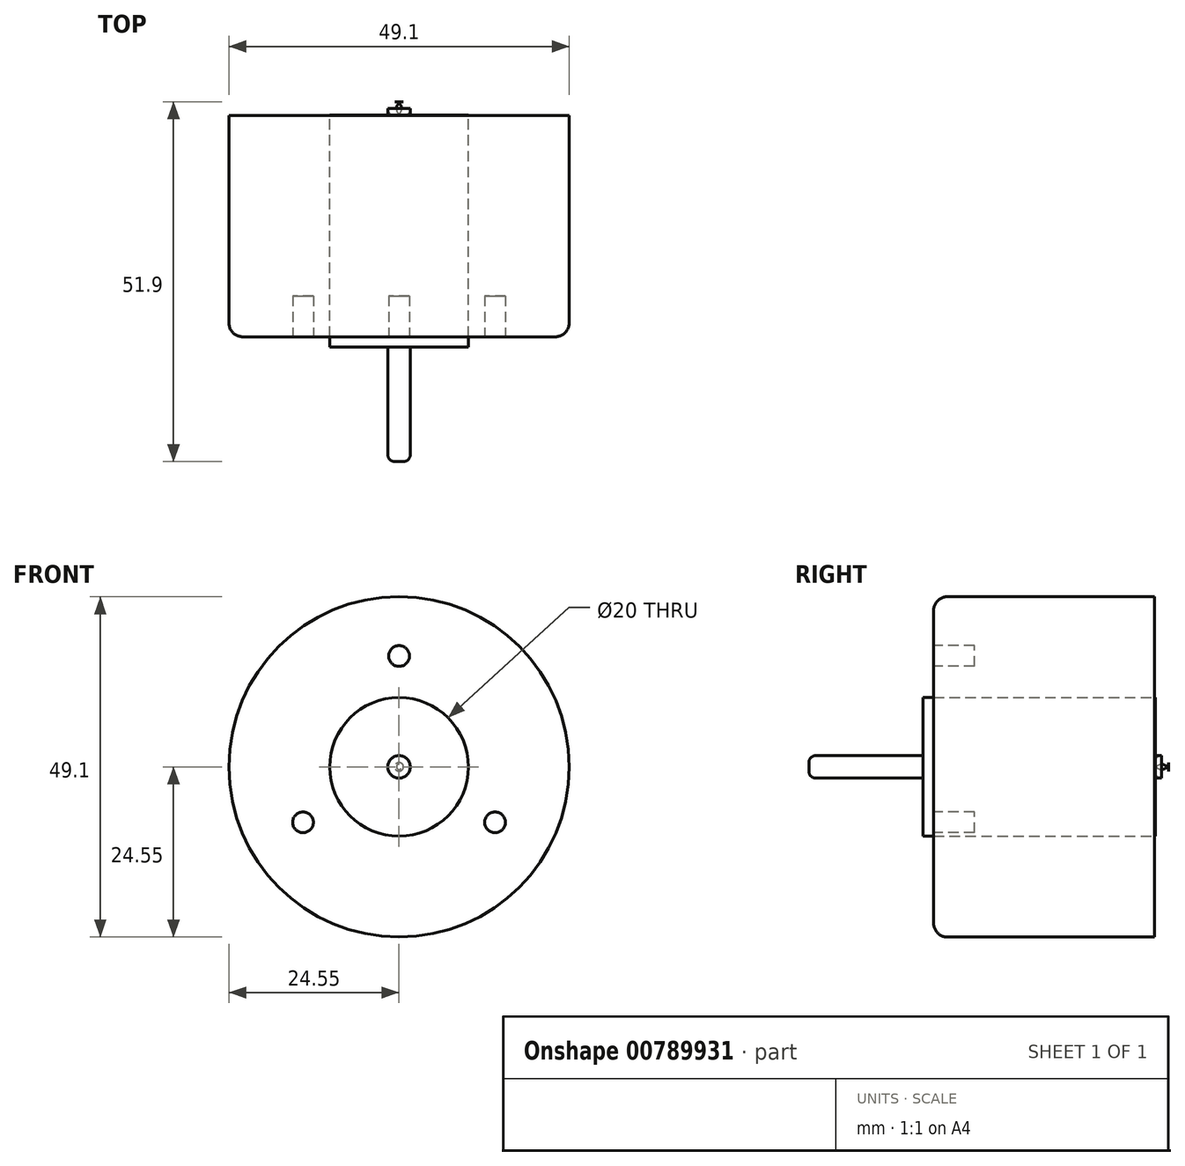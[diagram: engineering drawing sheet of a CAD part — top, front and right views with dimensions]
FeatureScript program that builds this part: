
annotation { "Feature Type Name" : "Feature", "Feature Type Description" : "" }
export const myFeature = defineFeature(function(context is Context, id is Id, definition is map)
    precondition{}
    {
        {
            var Q0;
            Q0=qCreatedBy(makeId("Front.planeOp"),FACE);
            var sketch = newSketch(context, id + "F0", { "sketchPlane" : qUnion([Q0])});
            skCircle(sketch, "E0", {"center": v(0, 0) * mm, "radius": 24.55 * mm});
            skCircle(sketch, "E1", {"center": v(0, 0) * mm, "radius": 10 * mm});
            skSolve(sketch);
        }
        {
            var Q0;
            Q0=makeQuery(id+"F0.imprint","IMPRINT",FACE,{"disambiguationData":[TD([[makeQuery(id+"F0.imprint","IMPRINT",EDGE,{"derivedFrom":sQuery(id+"F0.wireOp",EDGE,"E0")}),1.0]])]});
            extrude(context, id + "F1", {"entities" : qUnion([Q0]), "oppositeDirection" : true, "depth" : 31.9 * mm, "offsetDistance" : 25 * mm});
        }
        {
            var Q0;
            Q0=qCreatedBy(makeId("Front.planeOp"),FACE);
            var sketch = newSketch(context, id + "F2", { "sketchPlane" : qUnion([Q0])});
            skCircle(sketch, "E2", {"center": v(0, 0) * mm, "radius": 1.63 * mm});
            skCircle(sketch, "E3", {"center": v(0, 0) * mm, "radius": 10 * mm});
            skSolve(sketch);
        }
        {
            var Q0;
            Q0=makeQuery(id+"F2.imprint","IMPRINT",FACE,{"disambiguationData":[TD([[makeQuery(id+"F2.imprint","IMPRINT",EDGE,{"derivedFrom":sQuery(id+"F2.wireOp",EDGE,"E2")}),-1.0]])]});
            extrude(context, id + "F3", {"entities" : qUnion([Q0]), "depth" : 1.5 * mm, "offsetDistance" : 25 * mm, "hasSecondDirection" : true, "secondDirectionOppositeDirection" : true, "secondDirectionDepth" : 32 * mm});
        }
        {
            var Q0;
            Q0=qCreatedBy(makeId("Front.planeOp"),FACE);
            var sketch = newSketch(context, id + "F4", { "sketchPlane" : qUnion([Q0])});
            skCircle(sketch, "E4", {"center": v(0, 0) * mm, "radius": 1.63 * mm});
            skSolve(sketch);
        }
        {
            var Q0;
            Q0=makeQuery(id+"F4.imprint","IMPRINT",FACE,{"disambiguationData":[TD([[makeQuery(id+"F4.imprint","IMPRINT",EDGE,{"derivedFrom":sQuery(id+"F4.wireOp",EDGE,"E4")}),1.0]])]});
            extrude(context, id + "F5", {"entities" : qUnion([Q0]), "operationType" : NewBodyOperationType.ADD, "depth" : 18 * mm, "offsetDistance" : 25 * mm, "hasSecondDirection" : true, "secondDirectionOppositeDirection" : true, "secondDirectionDepth" : 33.9 * mm});
        }
        {
            var Q0;
            Q0=makeQuery(id+"F1.opExtrude","CAP_EDGE",EDGE,{"disambiguationData":[OSD([sQuery(id+"F0.wireOp",EDGE,"E0")])],"isStart":true});
            fillet(context, id + "F6", {"entities" : qUnion([Q0]), "radius" : 2 * mm, "tangentPropagation" : true, "allowEdgeOverflow" : false});
        }
        {
            var Q0;
            Q0=makeQuery(id+"F5.opExtrude","CAP_EDGE",EDGE,{"disambiguationData":[OSD([sQuery(id+"F4.wireOp",EDGE,"E4")])],"isStart":false});
            fillet(context, id + "F7", {"entities" : qUnion([Q0]), "radius" : 1 * mm, "tangentPropagation" : true, "allowEdgeOverflow" : false});
        }
        {
            var Q0;
            Q0=makeQuery(id+"F5.opExtrude","CAP_EDGE",EDGE,{"disambiguationData":[OSD([sQuery(id+"F4.wireOp",EDGE,"E4")])],"isStart":true});
            fillet(context, id + "F8", {"entities" : qUnion([Q0]), "radius" : 1 * mm, "tangentPropagation" : true, "allowEdgeOverflow" : false});
        }
        {
            var Q0;
            Q0=qCreatedBy(makeId("Front.planeOp"),FACE);
            var sketch = newSketch(context, id + "F9", { "sketchPlane" : qUnion([Q0])});
            skCircle(sketch, "E5", {"center": v(0, 16) * mm, "radius": 1.5 * mm});
            skCircle(sketch, "E6.1.0", {"center": v(-13.86, -8) * mm, "radius": 1.5 * mm});
            skCircle(sketch, "E6.2.0", {"center": v(13.86, -8) * mm, "radius": 1.5 * mm});
            skPoint(sketch, "E6.center", {"position": v(0, 0) * mm});
            skSolve(sketch);
        }
        {
            var Q0;
            Q0=makeQuery(id+"F9.imprint","IMPRINT",FACE,{"disambiguationData":[TD([[makeQuery(id+"F9.imprint","IMPRINT",EDGE,{"derivedFrom":sQuery(id+"F9.wireOp",EDGE,"E6.2.0")}),1.0]])]});
            var Q1;
            Q1=makeQuery(id+"F9.imprint","IMPRINT",FACE,{"disambiguationData":[TD([[makeQuery(id+"F9.imprint","IMPRINT",EDGE,{"derivedFrom":sQuery(id+"F9.wireOp",EDGE,"E6.1.0")}),1.0]])]});
            var Q2;
            Q2=makeQuery(id+"F9.imprint","IMPRINT",FACE,{"disambiguationData":[TD([[makeQuery(id+"F9.imprint","IMPRINT",EDGE,{"derivedFrom":sQuery(id+"F9.wireOp",EDGE,"E5")}),1.0]])]});
            extrude(context, id + "F10", {"entities" : qUnion([Q0, Q1, Q2]), "operationType" : NewBodyOperationType.REMOVE, "oppositeDirection" : true, "depth" : 5.9 * mm, "offsetDistance" : 25 * mm});
        }
    });
